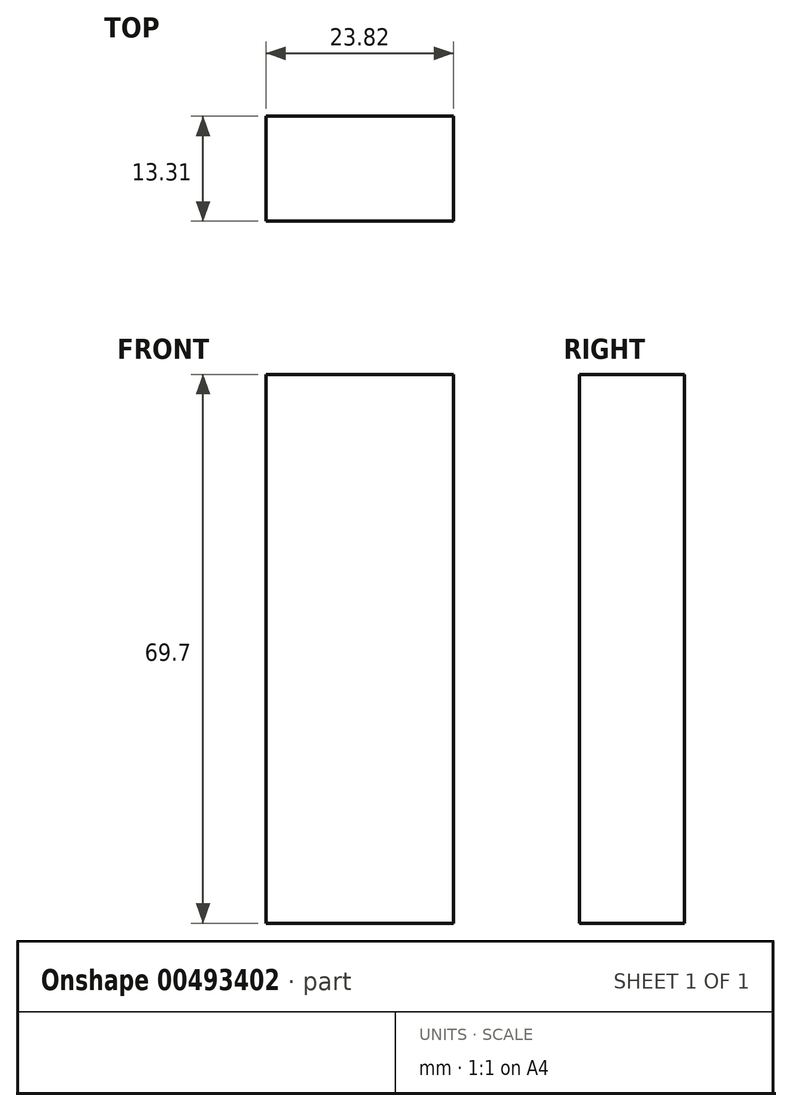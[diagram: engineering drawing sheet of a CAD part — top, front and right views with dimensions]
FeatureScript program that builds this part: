
annotation { "Feature Type Name" : "Feature", "Feature Type Description" : "" }
export const myFeature = defineFeature(function(context is Context, id is Id, definition is map)
    precondition{}
    {
        {
            var Q0;
            Q0=qCreatedBy(makeId("Front.planeOp"),FACE);
            var sketch = newSketch(context, id + "F0", { "sketchPlane" : qUnion([Q0])});
            skLineSegment(sketch, "E0.bottom", {"start": v(-11.91, 34.85) * mm, "end": v(11.91, 34.85) * mm});
            skLineSegment(sketch, "E0.top", {"start": v(-11.91, -34.85) * mm, "end": v(11.91, -34.85) * mm});
            skLineSegment(sketch, "E0.left", {"start": v(-11.91, 34.85) * mm, "end": v(-11.91, -34.85) * mm});
            skLineSegment(sketch, "E0.right", {"start": v(11.91, 34.85) * mm, "end": v(11.91, -34.85) * mm});
            skPoint(sketch, "E0.middle", {"position": v(0, 0) * mm});
            skSolve(sketch);
        }
        {
            var Q0;
            Q0=makeQuery(id+"F0.imprint","IMPRINT",FACE,{"disambiguationData":[TD([[makeQuery(id+"F0.imprint","IMPRINT",EDGE,{"derivedFrom":sQuery(id+"F0.wireOp",EDGE,"E0.bottom")}),-1.0]])]});
            extrude(context, id + "F1", {"entities" : qUnion([Q0]), "depth" : 13.3 * mm});
        }
    });
